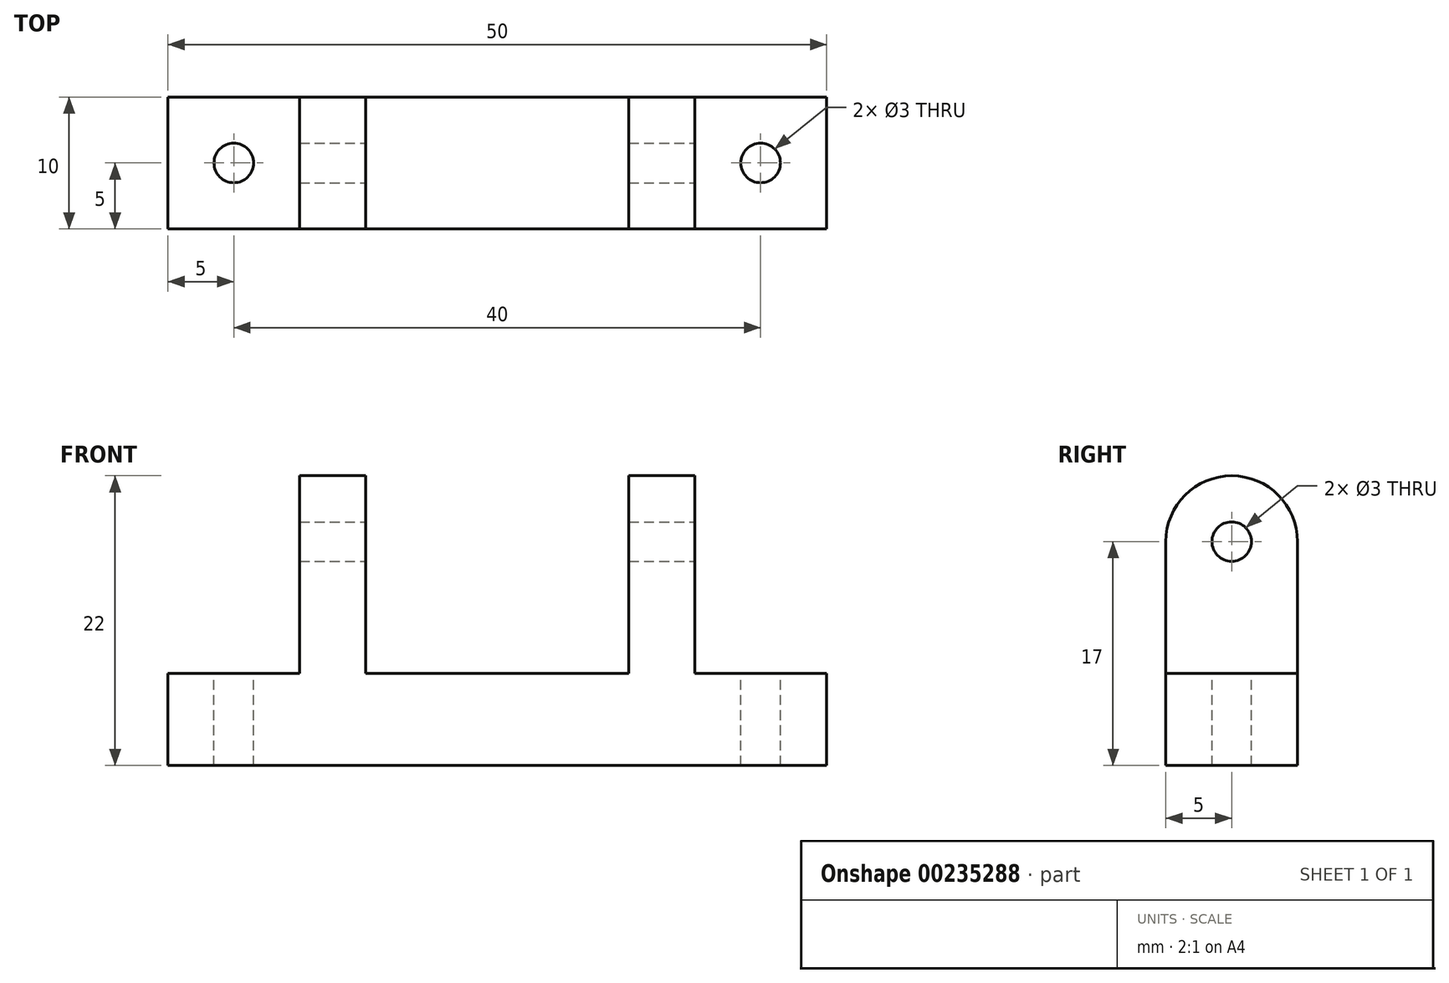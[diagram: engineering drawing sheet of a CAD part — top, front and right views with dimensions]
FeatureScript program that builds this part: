
annotation { "Feature Type Name" : "Feature", "Feature Type Description" : "" }
export const myFeature = defineFeature(function(context is Context, id is Id, definition is map)
    precondition{}
    {
        {
            var Q0;
            Q0=qCreatedBy(makeId("Top.planeOp"),FACE);
            var sketch = newSketch(context, id + "F0", { "sketchPlane" : qUnion([Q0])});
            skLineSegment(sketch, "E0.bottom", {"start": v(0, 0) * mm, "end": v(50, 0) * mm});
            skLineSegment(sketch, "E0.top", {"start": v(0, 10) * mm, "end": v(50, 10) * mm});
            skLineSegment(sketch, "E0.left", {"start": v(0, 0) * mm, "end": v(0, 10) * mm});
            skLineSegment(sketch, "E0.right", {"start": v(50, 0) * mm, "end": v(50, 10) * mm});
            skSolve(sketch);
        }
        {
            var Q0;
            Q0 = qSketchRegion(id + "F0", true);
            extrude(context, id + "F1", {"entities" : qUnion([Q0]), "depth" : 7 * mm});
        }
        {
            var Q0;
            Q0=makeQuery(id+"F1.opExtrude","CAP_FACE",FACE,{"disambiguationData":[OSD([sQuery(id+"F0.wireOp",EDGE,"E0.bottom"),sQuery(id+"F0.wireOp",EDGE,"E0.top"),sQuery(id+"F0.wireOp",EDGE,"E0.left"),sQuery(id+"F0.wireOp",EDGE,"E0.right")])],"isStart":false});
            var sketch = newSketch(context, id + "F2", { "sketchPlane" : qUnion([Q0])});
            skLineSegment(sketch, "E1.bottom", {"start": v(10, 0) * mm, "end": v(40, 0) * mm});
            skLineSegment(sketch, "E1.top", {"start": v(10, 10) * mm, "end": v(40, 10) * mm});
            skLineSegment(sketch, "E1.left", {"start": v(10, 0) * mm, "end": v(10, 10) * mm});
            skLineSegment(sketch, "E1.right", {"start": v(40, 0) * mm, "end": v(40, 10) * mm});
            skSolve(sketch);
        }
        {
            var Q0;
            {var subQ0=sQuery(id+"F2.wireOp",EDGE,"E1.right");Q0=makeQuery(id+"F2.imprint","IMPRINT",FACE,{"disambiguationData":[TD([[makeQuery(id+"F2.imprint","IMPRINT",EDGE,{"derivedFrom":subQ0}),-1.0]])]});}
            var sketch = newSketch(context, id + "F3", { "sketchPlane" : qUnion([Q0])});
            skCircle(sketch, "E2", {"center": v(45, 5) * mm, "radius": 1.5 * mm});
            skCircle(sketch, "E3", {"center": v(5, 5) * mm, "radius": 1.5 * mm});
            skSolve(sketch);
        }
        {
            var Q0;
            Q0 = qSketchRegion(id + "F2", true);
            extrude(context, id + "F4", {"entities" : qUnion([Q0]), "operationType" : NewBodyOperationType.ADD, "depth" : 15 * mm});
        }
        {
            var Q0;
            Q0=makeQuery(id+"F4.opExtrude","CAP_EDGE",EDGE,{"disambiguationData":[OSD([sQuery(id+"F2.wireOp",EDGE,"E1.top")])],"isStart":false});
            var Q1;
            Q1=makeQuery(id+"F4.opExtrude","CAP_EDGE",EDGE,{"disambiguationData":[OSD([sQuery(id+"F2.wireOp",EDGE,"E1.bottom")])],"isStart":false});
            fillet(context, id + "F5", {"entities" : qUnion([Q0, Q1]), "radius" : 5 * mm, "tangentPropagation" : true, "allowEdgeOverflow" : false});
        }
        {
            var Q0;
            Q0 = qSketchRegion(id + "F3", true);
            extrude(context, id + "F6", {"entities" : qUnion([Q0]), "operationType" : NewBodyOperationType.REMOVE, "oppositeDirection" : true, "depth" : 25 * mm});
        }
        {
            var Q0;
            Q0=makeQuery(id+"F4.opExtrude","SWEPT_FACE",FACE,{"disambiguationData":[OSD([sQuery(id+"F2.wireOp",EDGE,"E1.right")])]});
            var sketch = newSketch(context, id + "F7", { "sketchPlane" : qUnion([Q0])});
            skCircle(sketch, "E4", {"center": v(5, 17) * mm, "radius": 1.5 * mm});
            skSolve(sketch);
        }
        {
            var Q0;
            Q0 = qSketchRegion(id + "F7", true);
            extrude(context, id + "F8", {"entities" : qUnion([Q0]), "operationType" : NewBodyOperationType.REMOVE, "oppositeDirection" : true, "depth" : 50 * mm});
        }
        {
            var Q0;
            Q0=makeQuery(id+"F1.opExtrude","SWEPT_BODY",BODY,{"disambiguationData":[OSD([sQuery(id+"F0.wireOp",EDGE,"E0.bottom"),sQuery(id+"F0.wireOp",EDGE,"E0.top"),sQuery(id+"F0.wireOp",EDGE,"E0.left"),sQuery(id+"F0.wireOp",EDGE,"E0.right")])]});
            transform(context, id + "F9", {"entities" : qUnion([Q0]), "transformType" : TransformType.TRANSLATION_3D, "dx" : 0 * mm, "dy" : 0 * mm, "dz" : 40 * mm, "makeCopy" : true});
        }
        {
            var Q0;
            Q0=makeQuery(id+"F9.opPattern","COPY",FACE,{"derivedFrom":makeQuery(id+"F1.opExtrude","CAP_FACE",FACE,{"disambiguationData":[OSD([sQuery(id+"F0.wireOp",EDGE,"E0.bottom"),sQuery(id+"F0.wireOp",EDGE,"E0.top"),sQuery(id+"F0.wireOp",EDGE,"E0.left"),sQuery(id+"F0.wireOp",EDGE,"E0.right")])],"isStart":false}),"instanceName":"1"});
            var sketch = newSketch(context, id + "F10", { "sketchPlane" : qUnion([Q0])});
            skLineSegment(sketch, "E5.bottom", {"start": v(15, 10) * mm, "end": v(35, 10) * mm});
            skLineSegment(sketch, "E5.top", {"start": v(15, 0) * mm, "end": v(35, 0) * mm});
            skLineSegment(sketch, "E5.left", {"start": v(15, 10) * mm, "end": v(15, 0) * mm});
            skLineSegment(sketch, "E5.right", {"start": v(35, 10) * mm, "end": v(35, 0) * mm});
            skSolve(sketch);
        }
        {
            var Q0;
            Q0 = qSketchRegion(id + "F10", true);
            extrude(context, id + "F11", {"entities" : qUnion([Q0]), "operationType" : NewBodyOperationType.REMOVE, "depth" : 25 * mm});
        }
        {
            var Q0;
            Q0=makeQuery(id+"F1.opExtrude","SWEPT_BODY",BODY,{"disambiguationData":[OSD([sQuery(id+"F0.wireOp",EDGE,"E0.bottom"),sQuery(id+"F0.wireOp",EDGE,"E0.top"),sQuery(id+"F0.wireOp",EDGE,"E0.left"),sQuery(id+"F0.wireOp",EDGE,"E0.right")])]});
            deleteBodies(context, id + "F12", {"entities" : qUnion([Q0])});
        }
    });
